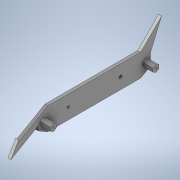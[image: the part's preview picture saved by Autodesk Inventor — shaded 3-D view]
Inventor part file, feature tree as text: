
AUTODESK INVENTOR PART (.ipt)
format: ipt  version: 2020 (Build 240168000, 168)  size: 182,272 bytes
history: native  units: in
note: dims shown in document units (in); Inventor stores cm internally (conversion verified against a paired STEP export)
features: other x3, extrude x2, sketch x2
ambient origin geometry x8: Origin, YZ Plane, XZ Plane, XY Plane, X Axis, Y Axis, Z Axis, Center Point
bodies: Solid1 (feature_tree)
feature tree (7):
  other  "HexWheelGuard.ipt"
  extrude  "Extrusion1"  TaperAngle=0.0deg  [1 undecoded]
  extrude  "Extrusion2"  Depth=0.3937in
  other  "Solid1::HexWheelGuard.ipt"
  other  "TaggingFeature1"
  sketch  "Sketch1"  dims[d0=0.3937in d6=0.0in d7=0.0in]
  sketch  "Sketch2"  dims[d9=0.315in d10=1.4843in d11=60.0deg d12=0.0787in d13=0.3937in d14=0.0in d20=0.3937in d21=0.5906in d22=1.1024in]
note: 1 required parameter value undecoded (feature->parameter linkage not recoverable at this tier; creation-order binding heuristic only, values carry confidence <= 0.55)
